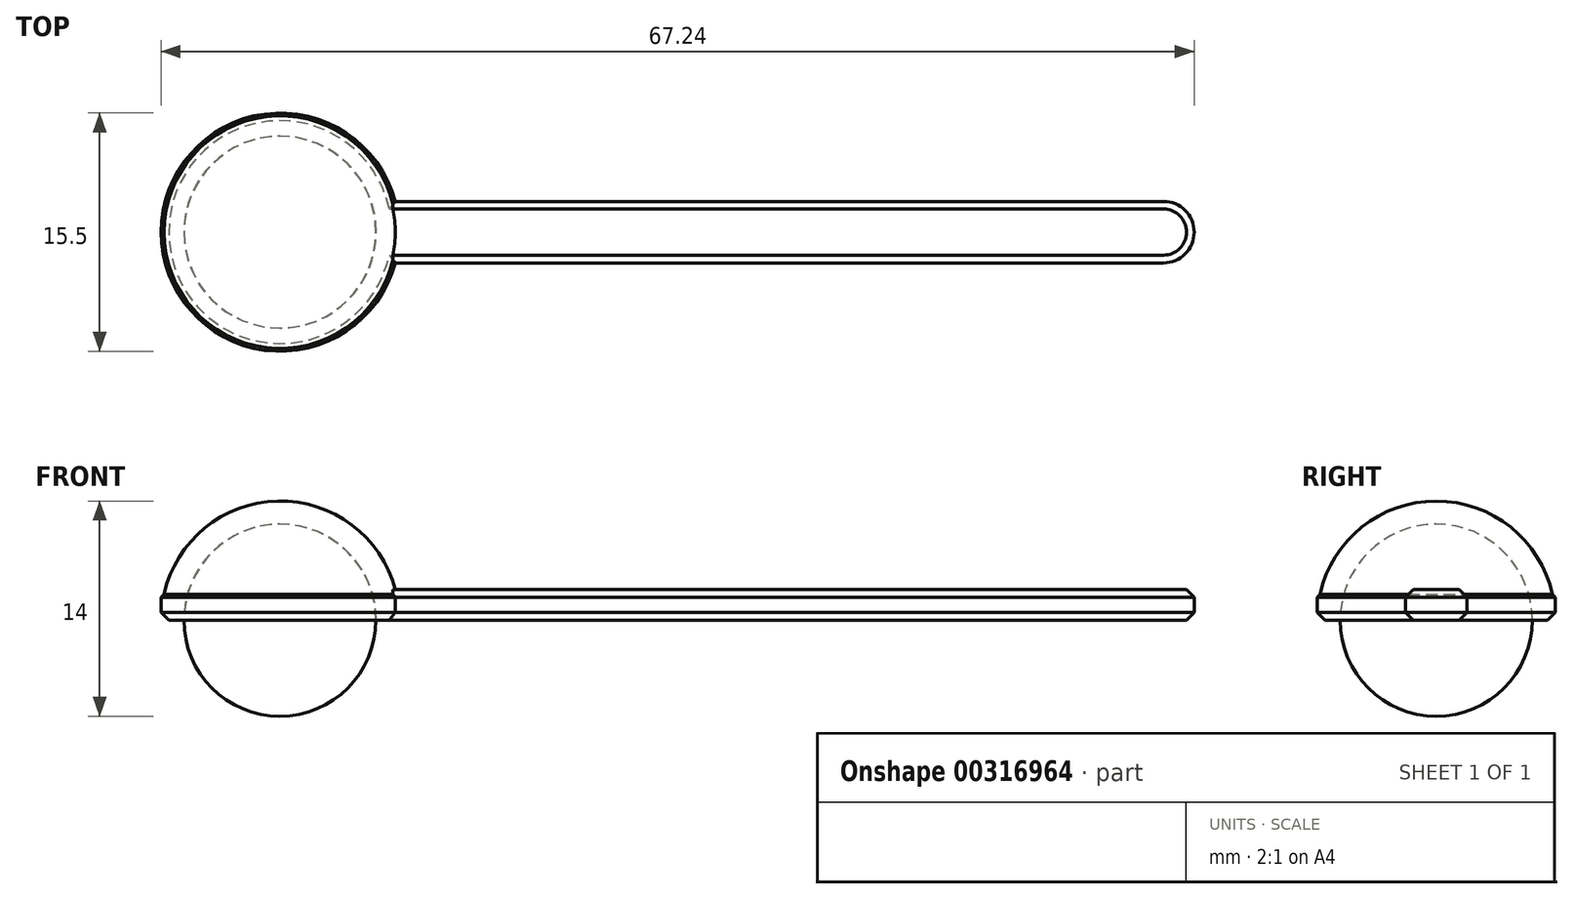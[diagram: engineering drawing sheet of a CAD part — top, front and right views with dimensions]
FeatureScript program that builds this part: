
annotation { "Feature Type Name" : "Feature", "Feature Type Description" : "" }
export const myFeature = defineFeature(function(context is Context, id is Id, definition is map)
    precondition{}
    {
        {
            var Q0;
            Q0=qCreatedBy(makeId("Top.planeOp"),FACE);
            var sketch = newSketch(context, id + "F0", { "sketchPlane" : qUnion([Q0])});
            skCircle(sketch, "E0", {"center": v(0, 0) * mm, "radius": 7.75 * mm});
            skLineSegment(sketch, "E1", {"start": v(7.49, 2) * mm, "end": v(57.49, 2) * mm});
            skLineSegment(sketch, "E2", {"start": v(-31.08, 0) * mm, "end": v(70.55, 0) * mm, "construction": true});
            skLineSegment(sketch, "E3.MirrorCS", {"start": v(7.49, -2) * mm, "end": v(57.49, -2) * mm});
            skArc(sketch, "E4", {"start": v(57.49, -2) * mm, "mid": v(59.49, 0) * mm, "end": v(57.49, 2) * mm});
            skCircle(sketch, "E5", {"center": v(0, 0) * mm, "radius": 6.25 * mm});
            skLineSegment(sketch, "E6", {"start": v(-7.75, 0) * mm, "end": v(7.75, 0) * mm});
            skSolve(sketch);
        }
        {
            var Q0;
            {var subQ1=sQuery(id+"F0.wireOp",EDGE,"E0");var subQ6=makeQuery(id+"F0.imprint","INTERSECT",VERTEX,{"derivedFrom":[subQ1,sQuery(id+"F0.wireOp",EDGE,"E1")]});Q0=makeQuery(id+"F0.imprint","IMPRINT",FACE,{"disambiguationData":[TD([[makeQuery(id+"F0.imprint","IMPRINT",EDGE,{"disambiguationData":[TD([[subQ6,1.0]])],"derivedFrom":subQ1}),1.0]])]});}
            var Q1;
            Q1=sQuery(id+"F0.wireOp",EDGE,"E2");
            revolve(context, id + "F1", {"entities" : qUnion([Q0]), "axis" : qUnion([Q1]), "revolveType" : RevolveType.ONE_DIRECTION, "angle" : 180 * degree});
        }
        {
            var Q0;
            {var subQ0=sQuery(id+"F0.wireOp",EDGE,"E1");Q0=makeQuery(id+"F0.imprint","IMPRINT",FACE,{"disambiguationData":[TD([[makeQuery(id+"F0.imprint","IMPRINT",EDGE,{"derivedFrom":subQ0}),-1.0]])]});}
            var Q1;
            {var subQ1=sQuery(id+"F0.wireOp",EDGE,"E0");var subQ6=makeQuery(id+"F0.imprint","INTERSECT",VERTEX,{"derivedFrom":[subQ1,sQuery(id+"F0.wireOp",EDGE,"E1")]});Q1=makeQuery(id+"F0.imprint","IMPRINT",FACE,{"disambiguationData":[TD([[makeQuery(id+"F0.imprint","IMPRINT",EDGE,{"disambiguationData":[TD([[subQ6,1.0]])],"derivedFrom":subQ1}),1.0]])]});}
            var Q2;
            {var subQ1=sQuery(id+"F0.wireOp",EDGE,"E0");var subQ6=makeQuery(id+"F0.imprint","INTERSECT",VERTEX,{"derivedFrom":[subQ1,sQuery(id+"F0.wireOp",EDGE,"E3.MirrorCS")]});Q2=makeQuery(id+"F0.imprint","IMPRINT",FACE,{"disambiguationData":[TD([[makeQuery(id+"F0.imprint","IMPRINT",EDGE,{"disambiguationData":[TD([[subQ6,1.0]])],"derivedFrom":subQ1}),1.0]])]});}
            extrude(context, id + "F2", {"entities" : qUnion([Q0, Q1, Q2]), "depth" : 2 * mm});
        }
        {
            var Q0;
            Q0=makeQuery(id+"F1.opRevolve","SWEPT_BODY",BODY,{"disambiguationData":[OSD([sQuery(id+"F0.wireOp",EDGE,"E0"),sQuery(id+"F0.wireOp",EDGE,"E5"),sQuery(id+"F0.wireOp",EDGE,"E6")])]});
            var Q1;
            Q1=makeQuery(id+"F2.opExtrude","SWEPT_BODY",BODY,{"disambiguationData":[OSD([sQuery(id+"F0.wireOp",EDGE,"E0"),sQuery(id+"F0.wireOp",EDGE,"E1"),sQuery(id+"F0.wireOp",EDGE,"E3.MirrorCS"),sQuery(id+"F0.wireOp",EDGE,"E4"),sQuery(id+"F0.wireOp",EDGE,"E5")])]});
            booleanBodies(context, id + "F3", {"operationType" : BooleanOperationType.UNION, "tools" : qUnion([Q0, Q1])});
        }
        {
            var Q0;
            Q0=qCreatedBy(makeId("Top.planeOp"),FACE);
            var sketch = newSketch(context, id + "F4", { "sketchPlane" : qUnion([Q0])});
            skArc(sketch, "E7", {"start": v(6.23, 0) * mm, "mid": v(-0.02, 6.25) * mm, "end": v(-6.27, 0) * mm});
            skLineSegment(sketch, "E8", {"start": v(6.23, 0) * mm, "end": v(-6.27, 0) * mm});
            skSolve(sketch);
        }
        {
            var Q0;
            Q0=makeQuery(id+"F4.imprint","IMPRINT",FACE,{"disambiguationData":[TD([[makeQuery(id+"F4.imprint","IMPRINT",EDGE,{"derivedFrom":sQuery(id+"F4.wireOp",EDGE,"E7")}),1.0]])]});
            var Q1;
            Q1=sQuery(id+"F0.wireOp",EDGE,"E2");
            revolve(context, id + "F5", {"entities" : qUnion([Q0]), "axis" : qUnion([Q1]), "revolveType" : RevolveType.FULL});
        }
        {
            var Q0;
            Q0=makeQuery(id+"F2.opExtrude","CAP_EDGE",EDGE,{"disambiguationData":[OSD([sQuery(id+"F0.wireOp",EDGE,"E4")])],"isStart":false});
            var Q1;
            Q1=makeQuery(id+"F2.opExtrude","CAP_EDGE",EDGE,{"disambiguationData":[OSD([sQuery(id+"F0.wireOp",EDGE,"E4")])],"isStart":true});
            var Q2;
            {var subQ0=sQuery(id+"F0.wireOp",EDGE,"E0");Q2=makeQuery(id+"F3.opBoolean","MERGE",EDGE,{"derivedFrom":[makeQuery(id+"F1.opRevolve","CAP_EDGE",EDGE,{"disambiguationData":[OSD([subQ0])],"isStart":true}),makeQuery(id+"F2.opExtrude","CAP_EDGE",EDGE,{"disambiguationData":[OSD([subQ0])],"isStart":true})]});}
            var Q3;
            Q3=makeQuery(id+"F2.opExtrude","CAP_EDGE",EDGE,{"disambiguationData":[OSD([sQuery(id+"F0.wireOp",EDGE,"E0")])],"isStart":false});
            chamfer(context, id + "F6", {"entities" : qUnion([Q0, Q1, Q2, Q3]), "width" : 0.5 * mm, "tangentPropagation" : true});
        }
    });
